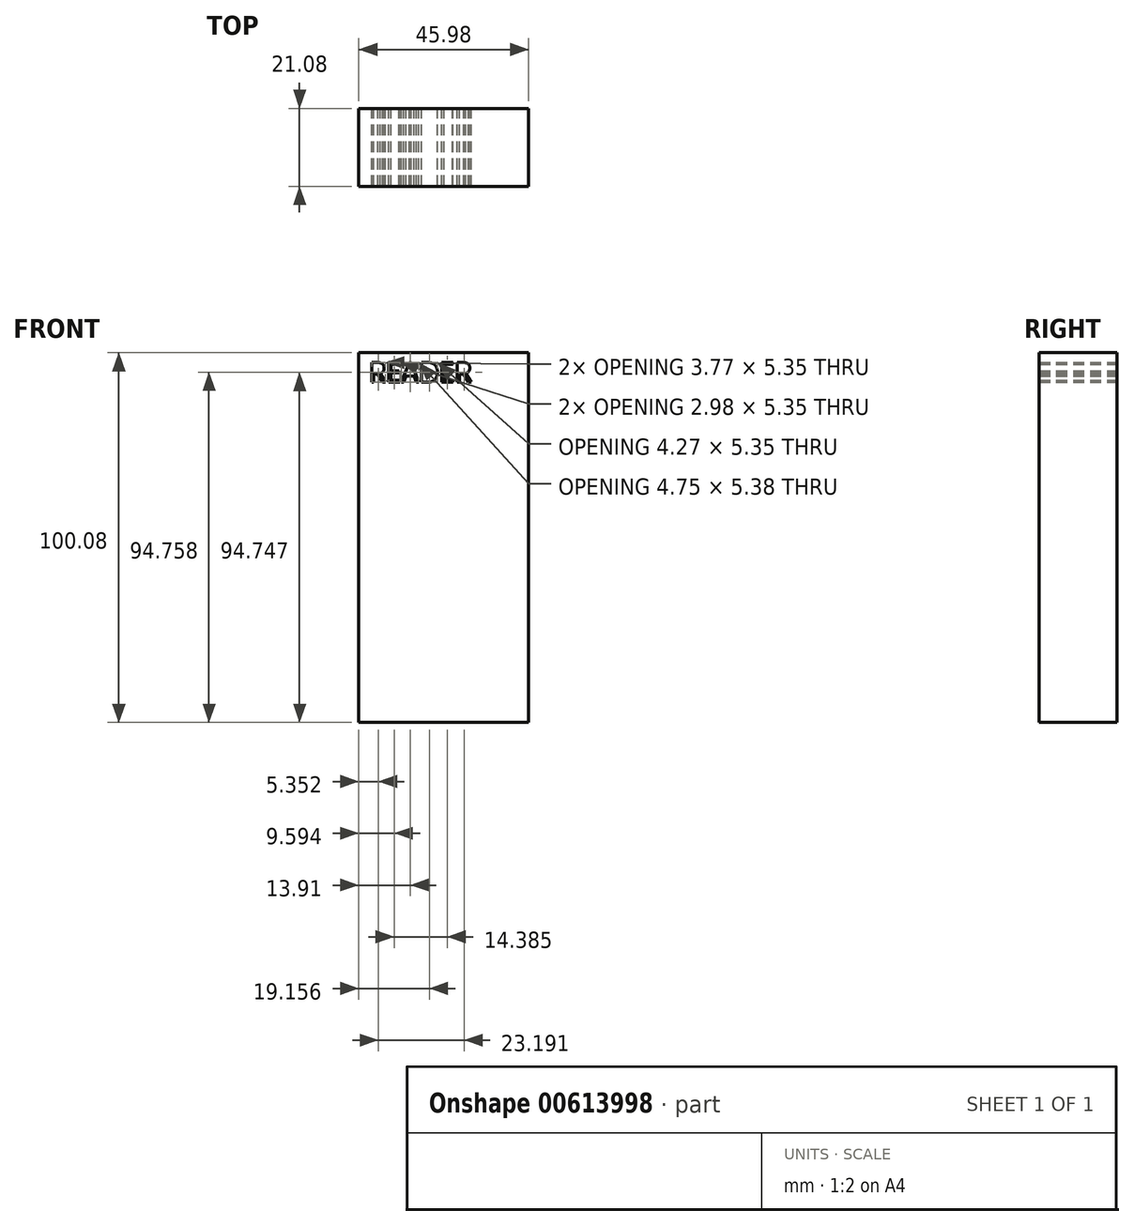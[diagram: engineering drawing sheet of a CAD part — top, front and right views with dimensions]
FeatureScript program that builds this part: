
annotation { "Feature Type Name" : "Feature", "Feature Type Description" : "" }
export const myFeature = defineFeature(function(context is Context, id is Id, definition is map)
    precondition{}
    {
        {
            var Q0;
            Q0=qCreatedBy(makeId("Front.planeOp"),FACE);
            var sketch = newSketch(context, id + "F0", { "sketchPlane" : qUnion([Q0])});
            skLineSegment(sketch, "E0.bottom", {"start": v(-22.99, 50.04) * mm, "end": v(22.99, 50.04) * mm});
            skLineSegment(sketch, "E0.top", {"start": v(-22.99, -50.04) * mm, "end": v(22.99, -50.04) * mm});
            skLineSegment(sketch, "E0.left", {"start": v(-22.99, 50.04) * mm, "end": v(-22.99, -50.04) * mm});
            skLineSegment(sketch, "E0.right", {"start": v(22.99, 50.04) * mm, "end": v(22.99, -50.04) * mm});
            skPoint(sketch, "E0.middle", {"position": v(0, 0) * mm});
            skText(sketch, "E1", { "text": "READER\n", "fontName": "OpenSans-Regular.ttf"});
            const initialGuessF0  = {"E1": [-0.02026, 0.04203, 1, 0, 0.0054]};
            skSetInitialGuess(sketch, initialGuessF0);
            skSolve(sketch);
        }
        {
            var Q0;
            Q0=makeQuery(id+"F0.imprint","IMPRINT",FACE,{"disambiguationData":[TD([[makeQuery(id+"F0.imprint","IMPRINT",EDGE,{"derivedFrom":sQuery(id+"F0.wireOp",EDGE,"E0.bottom")}),-1.0]])]});
            extrude(context, id + "F1", {"entities" : qUnion([Q0]), "depth" : 21.08 * mm, "offsetDistance" : 25.4 * mm});
        }
    });
